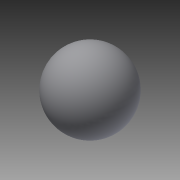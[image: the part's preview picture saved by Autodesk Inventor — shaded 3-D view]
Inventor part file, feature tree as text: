
AUTODESK INVENTOR PART (.ipt)
format: ipt  version: 2014 (Build 180170000, 170)  size: 97,792 bytes
history: native  units: in
note: dims shown in document units (in); Inventor stores cm internally (conversion verified against a paired STEP export)
features: revolve x1, sketch x1
ambient origin geometry x8: Origin, YZ Plane, XZ Plane, XY Plane, X Axis, Y Axis, Z Axis, Center Point
bodies: Solid1 (feature_tree)
feature tree (2):
  revolve  "Revolution1"  Angle=180.0deg
  sketch  "Sketch2"  dims[d1=24.0in d2=180.0deg]
